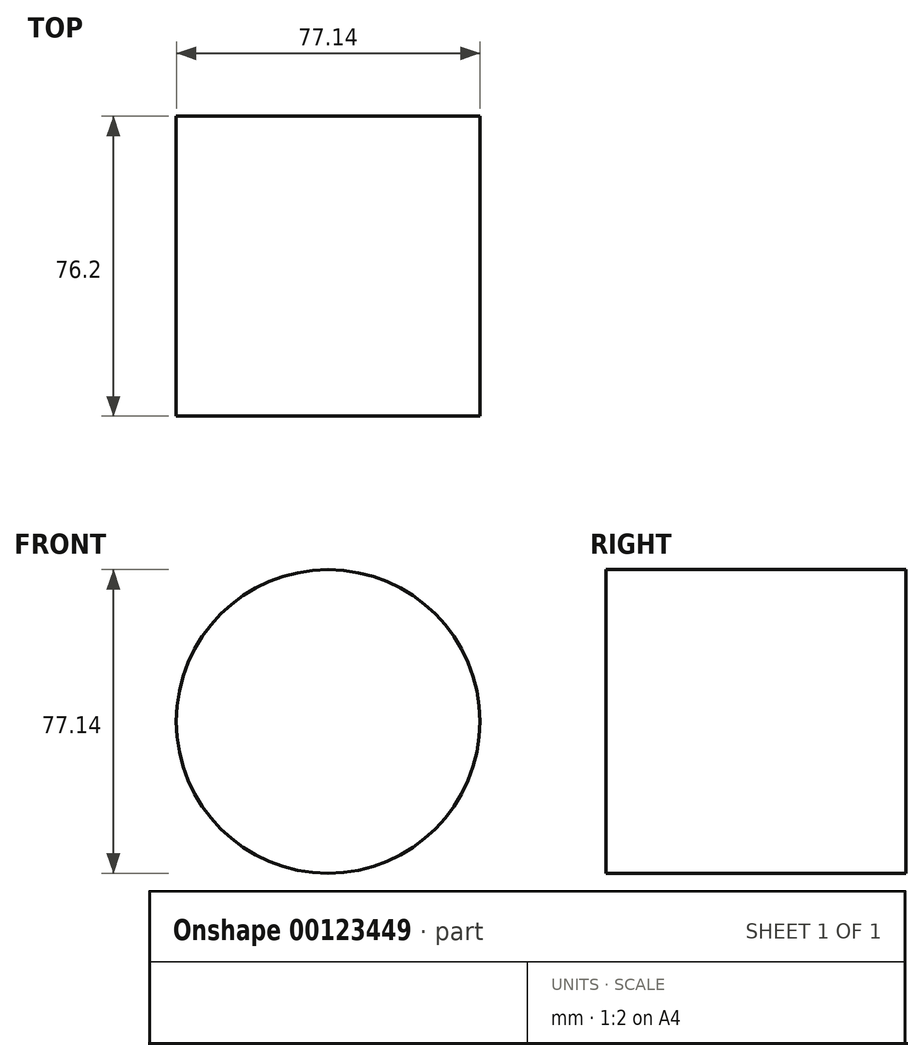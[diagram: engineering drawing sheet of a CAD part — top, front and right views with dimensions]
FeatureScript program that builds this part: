
annotation { "Feature Type Name" : "Feature", "Feature Type Description" : "" }
export const myFeature = defineFeature(function(context is Context, id is Id, definition is map)
    precondition{}
    {
        {
            var Q0;
            Q0=qCreatedBy(makeId("Front.planeOp"),FACE);
            var sketch = newSketch(context, id + "F0", { "sketchPlane" : qUnion([Q0])});
            skCircle(sketch, "E0", {"center": v(-53.86, 27.4) * mm, "radius": 38.57 * mm});
            skSolve(sketch);
        }
        {
            var Q0;
            Q0=makeQuery(id+"F0.imprint","IMPRINT",FACE,{"disambiguationData":[TD([[makeQuery(id+"F0.imprint","IMPRINT",EDGE,{"derivedFrom":sQuery(id+"F0.wireOp",EDGE,"E0")}),1.0]])]});
            extrude(context, id + "F1", {"entities" : qUnion([Q0]), "depth" : 25.4 * mm});
        }
        {
            var Q0;
            Q0=makeQuery(id+"F1.opExtrude","CAP_FACE",FACE,{"disambiguationData":[OSD([sQuery(id+"F0.wireOp",EDGE,"E0")])],"isStart":false});
            var Q1;
            Q1=makeQuery(id+"F1.opExtrude","CAP_FACE",FACE,{"disambiguationData":[OSD([sQuery(id+"F0.wireOp",EDGE,"E0")])],"isStart":true});
            extrude(context, id + "F2", {"entities" : qUnion([Q0, Q1]), "operationType" : NewBodyOperationType.ADD, "depth" : 25.4 * mm});
        }
        {
            var Q0;
            Q0=makeQuery(id+"F1.opExtrude","CAP_FACE",FACE,{"disambiguationData":[OSD([sQuery(id+"F0.wireOp",EDGE,"E0")])],"isStart":true});
            extrude(context, id + "F3", {"entities" : qUnion([Q0]), "operationType" : NewBodyOperationType.ADD, "depth" : 25.4 * mm});
        }
    });
